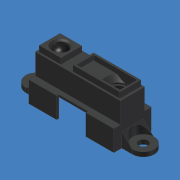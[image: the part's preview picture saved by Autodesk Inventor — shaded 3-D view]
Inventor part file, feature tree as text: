
AUTODESK INVENTOR PART (.ipt)
format: ipt  version: 2012 (Build 160160000, 160)  size: 267,776 bytes
history: native  units: mm (DEFAULTED — no unit token found)
features: sketch x12, extrude x7, hole x3, chamfer x3, revolve x2, shell x1, fillet x1, mirror x1
ambient origin geometry x8: Origin, YZ Plane, XZ Plane, XY Plane, X Axis, Y Axis, Z Axis, Center Point
bodies: Solid1 (feature_tree)
feature tree (30):
  extrude  "Extrusion1"  Depth=13.0mm
  extrude  "Extrusion2"  Depth=8.4mm
  extrude  "Extrusion3"  Depth=7.5mm
  hole  "Hole1"  [1 undecoded]
  chamfer  "Chamfer1"  Distance=2.0mm
  extrude  "Extrusion4"  Depth=0.5mm
  hole  "Hole2"  [1 undecoded]
  chamfer  "Chamfer3"  Distance=1.5mm
  chamfer  "Chamfer4"  Distance=1.5mm
  shell  "Shell1"  Thickness=0.75mm
  extrude  "Extrusion5"  Depth=1.7mm TaperAngle=0.0deg
  extrude  "Extrusion6"  Depth=1.5mm
  fillet  "Fillet1"  Radius=5.0mm
  extrude  "Extrusion7"  TaperAngle=45.0deg  [1 undecoded]
  hole  "Hole3"  [1 undecoded]
  mirror  "Mirror1"
  revolve  "Revolution2"  [1 undecoded]
  revolve  "Revolution3"  [1 undecoded]
  sketch  "Sketch1"  dims[d0=29.5mm d1=13.0mm]
  sketch  "Sketch2"  dims[d2=7.2mm d3=0.0mm d4=8.4mm]
  sketch  "Sketch3"  dims[d5=7.2mm d6=0.0mm d7=7.5mm]
  sketch  "Sketch4"  dims[d8=16.3mm d9=7.2mm]
  sketch  "Sketch5"  dims[d10=0.775mm]
  sketch  "Sketch6"  dims[d12=4.15mm d13=2.0mm d14=0.0mm]
  sketch  "Sketch7"  dims[d15=5.0mm d16=6.0mm d17=4.0mm d18=2.0mm d19=14.3117mm d20=1.5mm d21=0.0mm d22=0.5mm d23=2.0mm]
  sketch  "Sketch8"  dims[d24=0.6mm d25=1.7mm d26=0.0mm]
  sketch  "Sketch9"  dims[d27=20.0mm]
  sketch  "Sketch10"  dims[d28=5.0mm d29=6.0mm d30=6.0mm d31=2.0mm d32=14.3117mm d33=3.0mm d34=0.0mm d37=1.5mm d38=2.0mm d39=1.5mm d40=2.0mm d41=0.75mm]
  sketch  "Sketch15"  dims[d42=10.1mm d43=1.7mm d44=0.0mm]
  sketch  "Sketch16"  dims[d45=7.5mm d46=1.5mm d47=5.0mm d48=45.0deg d49=7.5mm d50=0.0mm d51=3.75mm d52=6.0mm d53=0.0mm d54=3.2mm d55=6.0mm d56=4.0mm d57=2.0mm d58=14.3117mm d59=8.0mm d60=20.594885mm d62=1.5mm d63=90.0deg d64=1.5mm d65=90.0deg d66=45.0deg d67=45.0deg d68=45.0deg]
note: 6 required parameter values undecoded (feature->parameter linkage not recoverable at this tier; creation-order binding heuristic only, values carry confidence <= 0.55)